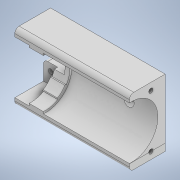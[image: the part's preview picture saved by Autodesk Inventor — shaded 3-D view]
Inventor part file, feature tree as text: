
AUTODESK INVENTOR PART (.ipt)
format: ipt  version: 2020 (Build 240168000, 168)  size: 308,736 bytes
history: native  units: in
note: dims shown in document units (in); Inventor stores cm internally (conversion verified against a paired STEP export)
features: extrude x6, sketch x6, plane x5, fillet x3, other x1
ambient origin geometry x8: Origin, YZ Plane, XZ Plane, XY Plane, X Axis, Y Axis, Z Axis, Center Point
bodies: Solid1 (feature_tree)
feature tree (21):
  extrude  "Extrusion1"  Depth=0.9843in TaperAngle=0.0deg
  extrude  "Extrusion2"  Depth=0.9213in
  plane  "Work Plane1"
  plane  "Work Plane2"
  extrude  "Extrusion3"  Depth=0.1969in
  plane  "Work Plane3"
  extrude  "Extrusion4"  Depth=0.1969in
  fillet  "Fillet1"  Radius=0.1969in
  plane  "Work Plane4"
  extrude  "Extrusion5"  TaperAngle=0.0deg  [1 undecoded]
  plane  "Work Plane5"
  extrude  "Extrusion6"  Depth=0.0197in
  fillet  "Fillet2"  [1 undecoded]
  fillet  "Fillet3"  Radius=0.1969in
  other  "Base motor"
  sketch  "Sketch8"  dims[d13=0.3937in d14=0.0in d15=0.0in]
  sketch  "Sketch3"  dims[d5=0.0in d6=0.9213in]
  sketch  "Sketch2"  dims[d1=0.1969in d2=0.0in d3=0.9843in d4=0.0in]
  sketch  "Sketch4"  dims[d7=0.0in d9=0.1969in]
  sketch  "Sketch7"  dims[d10=0.1969in d11=0.1969in d12=0.1969in]
  sketch  "Sketch9"  dims[d16=2.7559in d17=0.0in d18=0.1181in d19=0.0in d20=0.1969in d21=0.3937in d22=0.1969in d23=0.3937in d24=0.1181in d25=0.1181in d26=0.7874in d27=0.0in d28=1.9685in d29=0.7244in d30=0.125in d31=-0.9843in d32=0.1969in d33=0.1969in d34=1.9685in d35=0.7244in d36=0.125in d37=1.5748in d38=0.0in d39=0.0787in d40=0.0197in d8=0.0344in]
note: 2 required parameter values undecoded (feature->parameter linkage not recoverable at this tier; creation-order binding heuristic only, values carry confidence <= 0.55)
